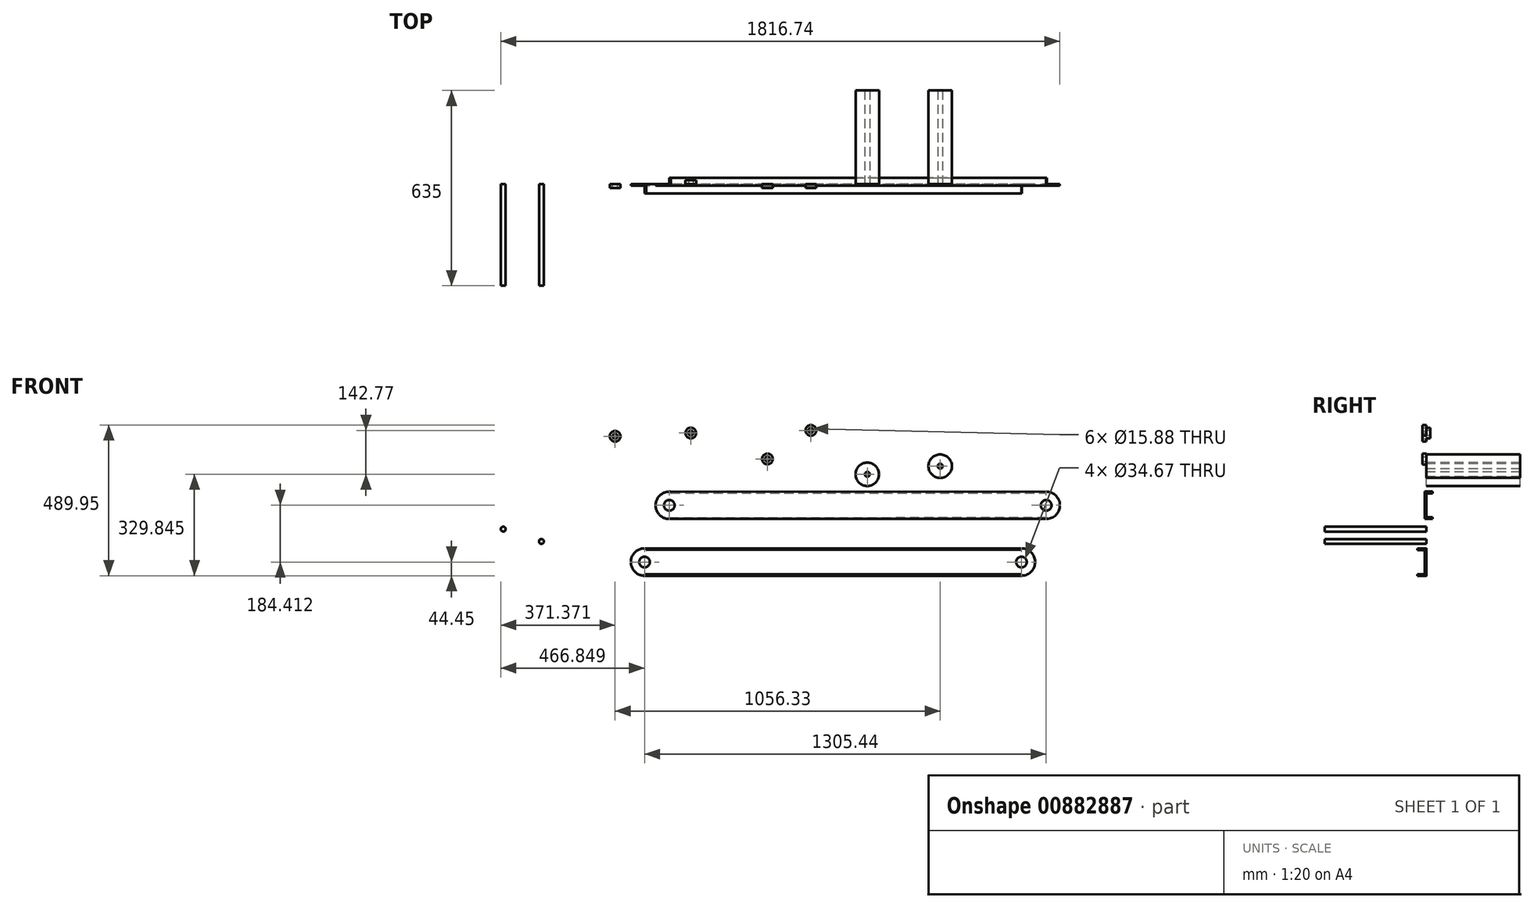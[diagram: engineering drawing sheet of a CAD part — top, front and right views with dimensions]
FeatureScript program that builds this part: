
annotation { "Feature Type Name" : "Feature", "Feature Type Description" : "" }
export const myFeature = defineFeature(function(context is Context, id is Id, definition is map)
    precondition{}
    {
        {
            var Q0;
            Q0=qCreatedBy(makeId("Front.planeOp"),FACE);
            var sketch = newSketch(context, id + "F0", { "sketchPlane" : qUnion([Q0])});
            skArc(sketch, "E0", {"start": v(148.44, -44.41) * mm, "mid": v(194.64, -0.88) * mm, "end": v(150.2, 44.45) * mm});
            skArc(sketch, "E1", {"start": v(-1069, 44.09) * mm, "mid": v(-1119.02, 2.83) * mm, "end": v(-1074.66, -44.45) * mm});
            skLineSegment(sketch, "E2", {"start": v(-1069, 44.09) * mm, "end": v(150.2, 44.45) * mm});
            skLineSegment(sketch, "E3", {"start": v(151.97, -44.41) * mm, "end": v(-1074.66, -44.45) * mm});
            skSolve(sketch);
        }
        {
            var Q0;
            Q0=makeQuery(id+"F0.imprint","IMPRINT",FACE,{"disambiguationData":[TD([[makeQuery(id+"F0.imprint","IMPRINT",EDGE,{"derivedFrom":sQuery(id+"F0.wireOp",EDGE,"DPMGJLlR-zqcN-m5ao-lYzB-VqvcgD4Ecf4p")}),1.0]])]});
            var Q1;
            {var subQ5=sQuery(id+"F0.wireOp",EDGE,"E1");Q1=makeQuery(id+"F0.imprint","IMPRINT",FACE,{"disambiguationData":[TD([[makeQuery(id+"F0.imprint","IMPRINT",EDGE,{"derivedFrom":subQ5}),1.0]])]});}
            extrude(context, id + "F1", {"entities" : qUnion([Q0, Q1]), "depth" : 4.78 * mm, "offsetDistance" : 25.4 * mm});
        }
        {
            var Q0;
            Q0=sQuery(id+"F0.wireOp",VERTEX,"E1.center");
            var Q1;
            Q1=sQuery(id+"F0.wireOp",VERTEX,"E0.center");
            var Q2;
            Q2=makeQuery(id+"F1.opExtrude","SWEPT_BODY",BODY,{"disambiguationData":[OSD([sQuery(id+"F0.wireOp",EDGE,"E0"),sQuery(id+"F0.wireOp",EDGE,"E1"),sQuery(id+"F0.wireOp",EDGE,"E2"),sQuery(id+"F0.wireOp",EDGE,"E3")])]});
            hole(context, id + "F2", {"style" : HoleStyle.SIMPLE, "endStyle" : HoleEndStyle.BLIND, "oppositeDirection" : true, "holeDiameter" : 34.67 * mm, "majorDiameter" : 6.35 * mm, "holeDepth" : 4.78 * mm, "isTappedThrough" : true, "tappedDepth" : 12.7 * mm, "tapClearance" : 3, "startFromSketch" : true, "locations" : qUnion([Q0, Q1]), "scope" : qUnion([Q2])});
        }
        {
            var Q0;
            Q0=makeQuery(id+"F1.opExtrude","CAP_FACE",FACE,{"disambiguationData":[OSD([sQuery(id+"F0.wireOp",EDGE,"E0"),sQuery(id+"F0.wireOp",EDGE,"E1"),sQuery(id+"F0.wireOp",EDGE,"E2"),sQuery(id+"F0.wireOp",EDGE,"E3")])],"isStart":false});
            var sketch = newSketch(context, id + "F3", { "sketchPlane" : qUnion([Q0])});
            skLineSegment(sketch, "E4", {"start": v(-1069, 44.09) * mm, "end": v(-1069, 39.31) * mm});
            skLineSegment(sketch, "E5", {"start": v(-1069, 39.31) * mm, "end": v(150.2, 39.67) * mm});
            skLineSegment(sketch, "E6", {"start": v(150.2, 39.67) * mm, "end": v(150.2, 44.45) * mm});
            skLineSegment(sketch, "E7", {"start": v(-1074.66, -44.45) * mm, "end": v(-1074.66, -39.67) * mm});
            skLineSegment(sketch, "E8", {"start": v(-1074.66, -39.67) * mm, "end": v(151.97, -39.64) * mm});
            skLineSegment(sketch, "E9", {"start": v(151.97, -44.41) * mm, "end": v(151.97, -39.64) * mm});
            skSolve(sketch);
        }
        {
            var Q0;
            Q0=makeQuery(id+"F3.imprint","IMPRINT",FACE,{"disambiguationData":[TD([[makeQuery(id+"F3.imprint","IMPRINT",EDGE,{"derivedFrom":sQuery(id+"F3.wireOp",EDGE,"E7")}),-1.0]])]});
            var Q1;
            Q1=makeQuery(id+"F3.imprint","IMPRINT",FACE,{"disambiguationData":[TD([[makeQuery(id+"F3.imprint","IMPRINT",EDGE,{"derivedFrom":sQuery(id+"F3.wireOp",EDGE,"E4")}),1.0]])]});
            extrude(context, id + "F4", {"entities" : qUnion([Q0, Q1]), "operationType" : NewBodyOperationType.ADD, "depth" : 25.4 * mm, "offsetDistance" : 25.4 * mm});
        }
        {
            var Q0;
            Q0=qCreatedBy(makeId("Front.planeOp"),FACE);
            var sketch = newSketch(context, id + "F5", { "sketchPlane" : qUnion([Q0])});
            skArc(sketch, "E10", {"start": v(229.01, 140) * mm, "mid": v(275.22, 183.54) * mm, "end": v(230.77, 228.86) * mm});
            skArc(sketch, "E11", {"start": v(-988.43, 228.5) * mm, "mid": v(-1038.44, 187.24) * mm, "end": v(-994.08, 139.96) * mm});
            skLineSegment(sketch, "E12", {"start": v(-988.43, 228.5) * mm, "end": v(230.77, 228.86) * mm});
            skLineSegment(sketch, "E13", {"start": v(232.55, 140) * mm, "end": v(-994.08, 139.96) * mm});
            skSolve(sketch);
        }
        {
            var Q0;
            {var subQ5=sQuery(id+"F5.wireOp",EDGE,"E11");Q0=makeQuery(id+"F5.imprint","IMPRINT",FACE,{"disambiguationData":[TD([[makeQuery(id+"F5.imprint","IMPRINT",EDGE,{"derivedFrom":subQ5}),1.0]])]});}
            extrude(context, id + "F6", {"entities" : qUnion([Q0]), "depth" : 4.78 * mm, "offsetDistance" : 25.4 * mm});
        }
        {
            var Q0;
            Q0=sQuery(id+"F5.wireOp",VERTEX,"E11.center");
            var Q1;
            Q1=sQuery(id+"F5.wireOp",VERTEX,"E10.center");
            var Q2;
            Q2=makeQuery(id+"F6.opExtrude","SWEPT_BODY",BODY,{"disambiguationData":[OSD([sQuery(id+"F5.wireOp",EDGE,"E10"),sQuery(id+"F5.wireOp",EDGE,"E11"),sQuery(id+"F5.wireOp",EDGE,"E12"),sQuery(id+"F5.wireOp",EDGE,"E13")])]});
            hole(context, id + "F7", {"style" : HoleStyle.SIMPLE, "endStyle" : HoleEndStyle.BLIND, "oppositeDirection" : true, "holeDiameter" : 34.67 * mm, "majorDiameter" : 6.35 * mm, "holeDepth" : 4.78 * mm, "isTappedThrough" : true, "tappedDepth" : 12.7 * mm, "tapClearance" : 3, "startFromSketch" : true, "locations" : qUnion([Q0, Q1]), "scope" : qUnion([Q2])});
        }
        {
            var Q0;
            Q0=makeQuery(id+"F6.opExtrude","CAP_FACE",FACE,{"disambiguationData":[OSD([sQuery(id+"F5.wireOp",EDGE,"E10"),sQuery(id+"F5.wireOp",EDGE,"E11"),sQuery(id+"F5.wireOp",EDGE,"E12"),sQuery(id+"F5.wireOp",EDGE,"E13")])],"isStart":false});
            var sketch = newSketch(context, id + "F8", { "sketchPlane" : qUnion([Q0])});
            skLineSegment(sketch, "E14", {"start": v(-988.43, 228.5) * mm, "end": v(-988.43, 223.73) * mm});
            skLineSegment(sketch, "E15", {"start": v(-988.43, 223.73) * mm, "end": v(230.77, 224.09) * mm});
            skLineSegment(sketch, "E16", {"start": v(230.77, 224.09) * mm, "end": v(230.77, 228.86) * mm});
            skLineSegment(sketch, "E17", {"start": v(-994.08, 139.96) * mm, "end": v(-994.08, 144.74) * mm});
            skLineSegment(sketch, "E18", {"start": v(-994.08, 144.74) * mm, "end": v(232.55, 145.1) * mm});
            skLineSegment(sketch, "E19", {"start": v(232.55, 145.1) * mm, "end": v(232.55, 140) * mm});
            skSolve(sketch);
        }
        {
            var Q0;
            Q0=makeQuery(id+"F8.imprint","IMPRINT",FACE,{"disambiguationData":[TD([[makeQuery(id+"F8.imprint","IMPRINT",EDGE,{"derivedFrom":sQuery(id+"F8.wireOp",EDGE,"E14")}),1.0]])]});
            var Q1;
            Q1=makeQuery(id+"F8.imprint","IMPRINT",FACE,{"disambiguationData":[TD([[makeQuery(id+"F8.imprint","IMPRINT",EDGE,{"derivedFrom":sQuery(id+"F8.wireOp",EDGE,"E17")}),-1.0]])]});
            extrude(context, id + "F9", {"entities" : qUnion([Q0, Q1]), "operationType" : NewBodyOperationType.ADD, "oppositeDirection" : true, "depth" : 25.4 * mm, "offsetDistance" : 25.4 * mm});
        }
        {
            var Q0;
            Q0=qCreatedBy(makeId("Front.planeOp"),FACE);
            var sketch = newSketch(context, id + "F10", { "sketchPlane" : qUnion([Q0])});
            skCircle(sketch, "E20", {"center": v(-675.26, 335.04) * mm, "radius": 17.34 * mm});
            skCircle(sketch, "E21", {"center": v(-675.26, 335.04) * mm, "radius": 7.94 * mm});
            skSolve(sketch);
        }
        {
            var Q0;
            Q0 = qSketchRegion(id + "F10", true);
            extrude(context, id + "F11", {"entities" : qUnion([Q0]), "depth" : 12.7 * mm, "offsetDistance" : 25.4 * mm});
        }
        {
            var Q0;
            Q0=makeQuery(id+"F11.opExtrude","CAP_FACE",FACE,{"disambiguationData":[OSD([sQuery(id+"F10.wireOp",EDGE,"E20"),sQuery(id+"F10.wireOp",EDGE,"E21")])],"isStart":true});
            var sketch = newSketch(context, id + "F12", { "sketchPlane" : qUnion([Q0])});
            skCircle(sketch, "E22", {"center": v(924.17, 419.34) * mm, "radius": 17.34 * mm});
            skCircle(sketch, "E23", {"center": v(924.17, 419.34) * mm, "radius": 7.94 * mm});
            skSolve(sketch);
        }
        {
            var Q0;
            Q0=makeQuery(id+"F12.imprint","IMPRINT",FACE,{"disambiguationData":[TD([[makeQuery(id+"F12.imprint","IMPRINT",EDGE,{"derivedFrom":sQuery(id+"F12.wireOp",EDGE,"E22")}),1.0]])]});
            var Q1;
            Q1=sQuery(id+"F12.wireOp",EDGE,"E23");
            extrude(context, id + "F13", {"entities" : qUnion([Q0]), "surfaceEntities" : qUnion([Q1]), "depth" : 12.7 * mm, "offsetDistance" : 25.4 * mm});
        }
        {
            var Q0;
            Q0=qCreatedBy(makeId("Front.planeOp"),FACE);
            var sketch = newSketch(context, id + "F14", { "sketchPlane" : qUnion([Q0])});
            skCircle(sketch, "E24", {"center": v(-534.15, 428.17) * mm, "radius": 17.34 * mm});
            skCircle(sketch, "E25", {"center": v(-534.15, 428.17) * mm, "radius": 7.94 * mm});
            skSolve(sketch);
        }
        {
            var Q0;
            Q0 = qSketchRegion(id + "F14", true);
            extrude(context, id + "F15", {"entities" : qUnion([Q0]), "depth" : 12.7 * mm, "offsetDistance" : 25.4 * mm});
        }
        {
            var Q0;
            Q0=qCreatedBy(makeId("Front.planeOp"),FACE);
            var sketch = newSketch(context, id + "F16", { "sketchPlane" : qUnion([Q0])});
            skCircle(sketch, "E26", {"center": v(0, 0) * mm, "radius": 17.34 * mm});
            skCircle(sketch, "E27", {"center": v(0, 0) * mm, "radius": 7.94 * mm});
            skCircle(sketch, "E28", {"center": v(-1170.14, 409.06) * mm, "radius": 17.34 * mm});
            skCircle(sketch, "E29", {"center": v(-1170.14, 409.06) * mm, "radius": 7.94 * mm});
            skSolve(sketch);
        }
        {
            var Q0;
            Q0=makeQuery(id+"F16.imprint","IMPRINT",FACE,{"disambiguationData":[TD([[makeQuery(id+"F16.imprint","IMPRINT",EDGE,{"derivedFrom":sQuery(id+"F16.wireOp",EDGE,"E28")}),1.0]])]});
            var Q1;
            Q1 = qConstructionFilter(qBodyType(qCreatedBy(id + "F16" ,EDGE), BodyType.WIRE), ConstructionObject.NO);
            extrude(context, id + "F17", {"entities" : qUnion([Q0]), "surfaceEntities" : qUnion([Q1]), "depth" : 12.7 * mm, "offsetDistance" : 25.4 * mm});
        }
        {
            var Q0;
            Q0=qCreatedBy(makeId("Front.planeOp"),FACE);
            var sketch = newSketch(context, id + "F18", { "sketchPlane" : qUnion([Q0])});
            skCircle(sketch, "E30", {"center": v(-350.75, 285.4) * mm, "radius": 38.1 * mm});
            skCircle(sketch, "E31", {"center": v(-350.75, 285.4) * mm, "radius": 7.94 * mm});
            skSolve(sketch);
        }
        {
            var Q0;
            Q0 = qSketchRegion(id + "F18", true);
            extrude(context, id + "F19", {"entities" : qUnion([Q0]), "oppositeDirection" : true, "depth" : 304.8 * mm, "offsetDistance" : 25.4 * mm});
        }
        {
            var Q0;
            Q0=qCreatedBy(makeId("Front.planeOp"),FACE);
            var sketch = newSketch(context, id + "F20", { "sketchPlane" : qUnion([Q0])});
            skCircle(sketch, "E32", {"center": v(-113.81, 311.7) * mm, "radius": 38.1 * mm});
            skCircle(sketch, "E33", {"center": v(-113.81, 311.7) * mm, "radius": 7.94 * mm});
            skSolve(sketch);
        }
        {
            var Q0;
            Q0 = qSketchRegion(id + "F20", true);
            extrude(context, id + "F21", {"entities" : qUnion([Q0]), "oppositeDirection" : true, "depth" : 304.8 * mm, "offsetDistance" : 25.4 * mm});
        }
        {
            var Q0;
            Q0=qCreatedBy(makeId("Front.planeOp"),FACE);
            var sketch = newSketch(context, id + "F22", { "sketchPlane" : qUnion([Q0])});
            skCircle(sketch, "E34", {"center": v(-1409.64, 67.07) * mm, "radius": 7.94 * mm});
            skSolve(sketch);
        }
        {
            var Q0;
            Q0 = qSketchRegion(id + "F22", true);
            extrude(context, id + "F23", {"entities" : qUnion([Q0]), "depth" : 330.2 * mm, "offsetDistance" : 25.4 * mm});
        }
        {
            var Q0;
            Q0=qCreatedBy(makeId("Front.planeOp"),FACE);
            var sketch = newSketch(context, id + "F24", { "sketchPlane" : qUnion([Q0])});
            skCircle(sketch, "E35", {"center": v(-1533.57, 107.03) * mm, "radius": 7.94 * mm});
            skSolve(sketch);
        }
        {
            var Q0;
            Q0 = qSketchRegion(id + "F24", true);
            extrude(context, id + "F25", {"entities" : qUnion([Q0]), "depth" : 330.2 * mm, "offsetDistance" : 25.4 * mm});
        }
    });
